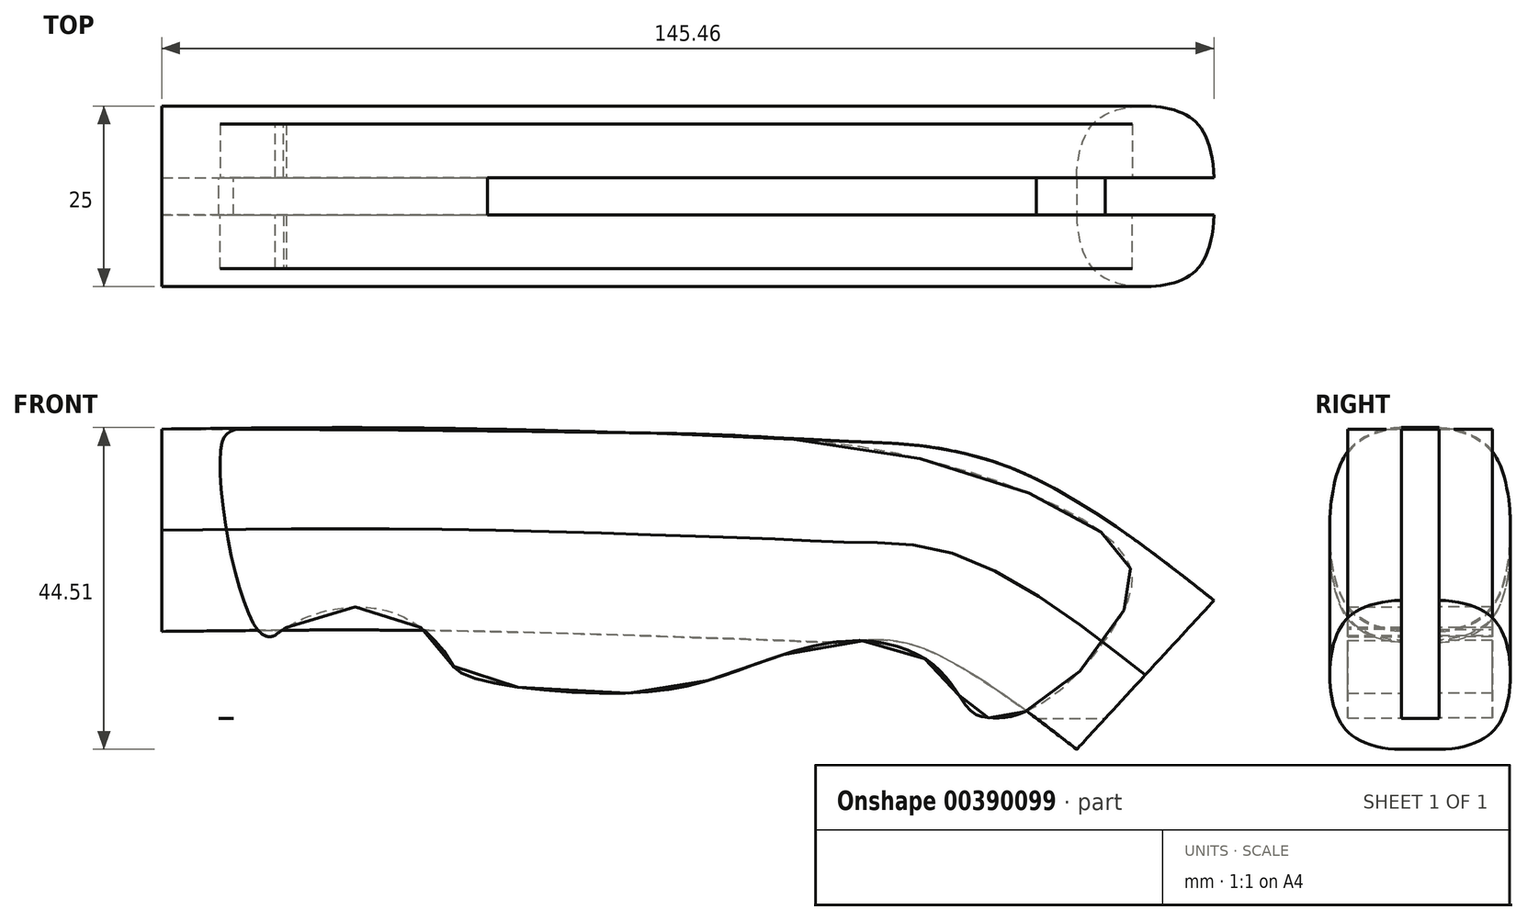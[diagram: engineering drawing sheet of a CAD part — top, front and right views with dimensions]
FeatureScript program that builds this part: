
annotation { "Feature Type Name" : "Feature", "Feature Type Description" : "" }
export const myFeature = defineFeature(function(context is Context, id is Id, definition is map)
    precondition{}
    {
        {
            var Q0;
            Q0=qCreatedBy(makeId("Front.planeOp"),FACE);
            var sketch = newSketch(context, id + "F0", { "sketchPlane" : qUnion([Q0])});
            skLineSegment(sketch, "E0", {"start": v(0, 40) * mm, "end": v(-250, 40) * mm});
            skLineSegment(sketch, "E1", {"start": v(-250, 40) * mm, "end": v(-250, 0) * mm});
            skLineSegment(sketch, "E2", {"start": v(-250, 0) * mm, "end": v(0, 0) * mm});
            skLineSegment(sketch, "E3", {"start": v(0, 0) * mm, "end": v(0, 40) * mm});
            skSolve(sketch);
        }
        {
            var Q0;
            Q0=qCreatedBy(makeId("Front.planeOp"),FACE);
            var sketch = newSketch(context, id + "F1", { "sketchPlane" : qUnion([Q0])});
            skLineSegment(sketch, "E4", {"start": v(-140.13, 40) * mm, "end": v(-10.13, 40) * mm, "construction": true});
            skLineSegment(sketch, "E5", {"start": v(-10.13, 40) * mm, "end": v(-10.13, 0) * mm, "construction": true});
            skFitSpline(sketch, "E6", {"points": [v(-195.15, 40) * mm, v(-214.61, 38.5) * mm, v(-226.5, 36.65) * mm, v(-250, 29) * mm], "startDerivative": vector(-36.4, 0) * mm, "endDerivative": vector(-83.44, -41.3) * mm});
            skLineSegment(sketch, "E7", {"start": v(-250, 40) * mm, "end": v(-250, 29) * mm, "construction": true});
            skFitSpline(sketch, "E8", {"points": [v(-250, 29) * mm, v(-237.9, 14.88) * mm, v(-219.9, 6.53) * mm, v(-197.47, 2.44) * mm, v(-140.13, -0.02) * mm], "startDerivative": vector(33.25, -72.74) * mm, "endDerivative": vector(161.21, 0) * mm});
            skFitSpline(sketch, "E9", {"points": [v(-140.13, -0.02) * mm, v(-137.85, 7.38) * mm, v(-129.23, 14.28) * mm, v(-117.32, 14.35) * mm, v(-110.68, 8.8) * mm, v(-108.34, 6.11) * mm, v(-85.42, 3.47) * mm, v(-71.01, 6.36) * mm, v(-55.73, 10.69) * mm, v(-45.11, 8.6) * mm, v(-40.68, 4.49) * mm, v(-37.73, 0.68) * mm, v(-32.41, 0.28) * mm, v(-22.8, 4.17) * mm, v(-12.46, 13.56) * mm, v(-11.48, 17.06) * mm, v(-13.01, 19.89) * mm, v(-23.92, 28.18) * mm, v(-50.74, 37.07) * mm, v(-90.96, 39.53) * mm, v(-140.13, 40) * mm], "startDerivative": vector(3.13, 131.36) * mm, "endDerivative": vector(-602.52, 0) * mm});
            skLineSegment(sketch, "E10", {"start": v(-195.15, 40) * mm, "end": v(-140.13, 40) * mm});
            skLineSegment(sketch, "E11", {"start": v(-140.13, 40) * mm, "end": v(-142.13, 40) * mm});
            skLineSegment(sketch, "E12", {"start": v(-142.13, 40) * mm, "end": v(-142.13, -0.02) * mm});
            skSolve(sketch);
        }
        {
            var Q0;
            Q0=qCreatedBy(makeId("Front.planeOp"),FACE);
            var sketch = newSketch(context, id + "F2", { "sketchPlane" : qUnion([Q0])});
            skFitSpline(sketch, "E13", {"points": [v(-139.83, 0) * mm, v(-137.7, 7.55) * mm, v(-129.23, 14.28) * mm, v(-117.32, 14.35) * mm, v(-110.68, 8.8) * mm, v(-108.34, 6.11) * mm, v(-85.42, 3.47) * mm, v(-71.01, 6.36) * mm, v(-55.73, 10.69) * mm, v(-45.11, 8.6) * mm, v(-40.68, 4.49) * mm, v(-37.73, 0.68) * mm, v(-35.14, 0.02) * mm, v(-32.41, 0.28) * mm, v(-25.38, 4.26) * mm, v(-16.97, 14.98) * mm, v(-15.84, 19.55) * mm, v(-17.11, 22.79) * mm, v(-23.92, 28.18) * mm, v(-50.74, 37.07) * mm, v(-90.96, 39.53) * mm, v(-139.08, 40) * mm], "startDerivative": vector(3.14, 131.36) * mm, "endDerivative": vector(-602.52, 0) * mm});
            skFitSpline(sketch, "E14", {"points": [v(-139.08, 40) * mm, v(-140.85, 39.45) * mm, v(-141.8, 37.79) * mm, v(-140.36, 22.3) * mm, v(-136.2, 11.67) * mm, v(-134.7, 11.32) * mm, v(-133.98, 11.7) * mm, v(-132.8, 12.56) * mm], "startDerivative": vector(-24.87, 0.07) * mm, "endDerivative": vector(13.86, 8) * mm});
            skSolve(sketch);
        }
        {
            var Q0;
            Q0=qCreatedBy(makeId("Front.planeOp"),FACE);
            var sketch = newSketch(context, id + "F3", { "sketchPlane" : qUnion([Q0])});
            skFitSpline(sketch, "E15", {"points": [v(-141.52, 25.66) * mm, v(-111.48, 25.66) * mm, v(-71.98, 24.55) * mm, v(-50, 23.16) * mm, v(-32.48, 18.15) * mm, v(-8.01, 0) * mm], "startDerivative": vector(127.42, 1.18) * mm, "endDerivative": vector(72.27, -65.29) * mm});
            skSolve(sketch);
        }
        {
            var Q0;
            Q0=qCreatedBy(makeId("Right.planeOp"),FACE);
            cPlane(context, id + "F4", {"entities" : qUnion([Q0]), "cplaneType" : CPlaneType.OFFSET, "offset" : 150 * mm, "oppositeDirection" : true, "width" : 150 * mm, "height" : 150 * mm});
        }
        {
            var Q0;
            Q0=qCreatedBy(id+"F4.planeOp",FACE);
            var sketch = newSketch(context, id + "F5", { "sketchPlane" : qUnion([Q0])});
            skLineSegment(sketch, "E16", {"start": v(0, 40) * mm, "end": v(0, 26) * mm, "construction": true});
            skLineSegment(sketch, "E17", {"start": v(0, 26) * mm, "end": v(12.5, 26) * mm, "construction": true});
            skFitSpline(sketch, "E18", {"points": [v(2.6, 40) * mm, v(8.74, 38) * mm, v(11.41, 33.88) * mm, v(12.5, 26) * mm], "startDerivative": vector(21.5, 0.1) * mm, "endDerivative": vector(-0.14, -22.75) * mm});
            skFitSpline(sketch, "E19.MirrorCS", {"points": [v(2.6, 12) * mm, v(8.74, 14) * mm, v(11.41, 18.12) * mm, v(12.5, 26) * mm], "startDerivative": vector(21.5, -0.1) * mm, "endDerivative": vector(-0.14, 22.75) * mm});
            skLineSegment(sketch, "E20.MirrorCS", {"start": v(0, 12) * mm, "end": v(0, 26) * mm, "construction": true});
            skFitSpline(sketch, "E21.MirrorCS", {"points": [v(2.6, 40) * mm, v(8.74, 38) * mm, v(11.41, 33.88) * mm, v(12.5, 26) * mm], "startDerivative": vector(21.5, 0.1) * mm, "endDerivative": vector(-0.14, -22.75) * mm});
            skFitSpline(sketch, "E22.MirrorCS", {"points": [v(-2.6, 40) * mm, v(-8.74, 38) * mm, v(-11.41, 33.88) * mm, v(-12.5, 26) * mm], "startDerivative": vector(-21.5, 0.1) * mm, "endDerivative": vector(0.14, -22.75) * mm});
            skFitSpline(sketch, "E23.MirrorCS", {"points": [v(-2.6, 12) * mm, v(-8.74, 14) * mm, v(-11.41, 18.12) * mm, v(-12.5, 26) * mm], "startDerivative": vector(-21.5, -0.1) * mm, "endDerivative": vector(0.14, 22.75) * mm});
            skLineSegment(sketch, "E24", {"start": v(2.6, 12) * mm, "end": v(-2.6, 12) * mm});
            skLineSegment(sketch, "E25", {"start": v(2.6, 40) * mm, "end": v(-2.6, 40) * mm});
            skSolve(sketch);
        }
        {
            var Q0;
            Q0=makeQuery(id+"F5.imprint","IMPRINT",FACE,{"disambiguationData":[TD([[makeQuery(id+"F5.imprint","IMPRINT",EDGE,{"derivedFrom":sQuery(id+"F5.wireOp",EDGE,"E19.MirrorCS")}),1.0]])]});
            var Q1;
            Q1=sQuery(id+"F3.wireOp",EDGE,"E15");
            sweep(context, id + "F6", {"profiles" : qUnion([Q0]), "path" : qUnion([Q1])});
        }
        {
            var Q0;
            Q0=makeQuery(id+"F1.imprint","IMPRINT",FACE,{"disambiguationData":[TD([[makeQuery(id+"F1.imprint","IMPRINT",EDGE,{"derivedFrom":sQuery(id+"F1.wireOp",EDGE,"E6")}),1.0]])]});
            extrude(context, id + "F7", {"entities" : qUnion([Q0]), "endBound" : BoundingType.SYMMETRIC, "depth" : 5.2 * mm});
        }
        {
            var Q0;
            Q0=makeQuery(id+"F7.opExtrude","CAP_EDGE",EDGE,{"disambiguationData":[OSD([sQuery(id+"F1.wireOp",EDGE,"E8")])],"isStart":false});
            var Q1;
            Q1=makeQuery(id+"F7.opExtrude","CAP_EDGE",EDGE,{"disambiguationData":[OSD([sQuery(id+"F1.wireOp",EDGE,"E8")])],"isStart":true});
            chamfer(context, id + "F8", {"entities" : qUnion([Q0, Q1]), "chamferType" : ChamferType.TWO_OFFSETS, "width1" : 20 * mm, "oppositeDirection" : false, "width2" : 2.6 * mm, "tangentPropagation" : true});
        }
        {
            var Q0;
            {var subQ0=sQuery(id+"F1.wireOp",EDGE,"E9");Q0=makeQuery(id+"F1.imprint","IMPRINT",FACE,{"disambiguationData":[TD([[makeQuery(id+"F1.imprint","IMPRINT",EDGE,{"derivedFrom":subQ0}),1.0]])]});}
            extrude(context, id + "F9", {"entities" : qUnion([Q0]), "operationType" : NewBodyOperationType.ADD, "endBound" : BoundingType.SYMMETRIC, "depth" : 5.2 * mm});
        }
        {
            var Q0;
            Q0=makeQuery(id+"F2.imprint","IMPRINT",FACE,{"disambiguationData":[TD([[makeQuery(id+"F2.imprint","IMPRINT",EDGE,{"derivedFrom":sQuery(id+"F2.wireOp",EDGE,"E13")}),1.0]])]});
            extrude(context, id + "F10", {"entities" : qUnion([Q0]), "endBound" : BoundingType.SYMMETRIC, "depth" : 20 * mm});
        }
        {
            var Q0;
            Q0=qSketchRegion(id+"F0",true);
            extrude(context, id + "F11", {"entities" : qUnion([Q0]), "operationType" : NewBodyOperationType.REMOVE, "endBound" : BoundingType.SYMMETRIC, "depth" : 5.2 * mm});
        }
    });
